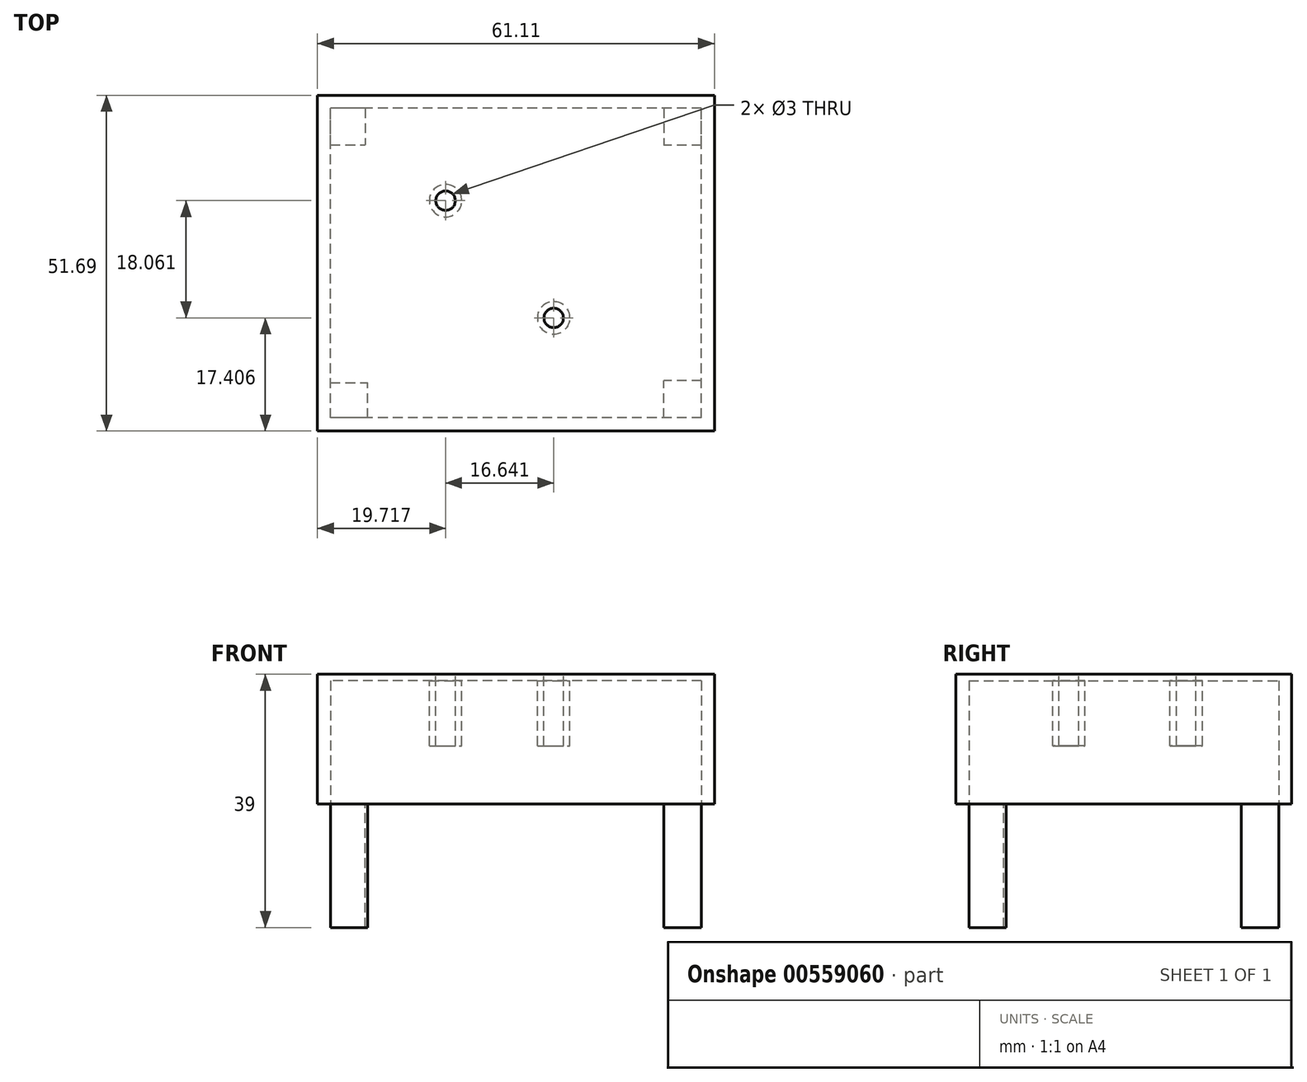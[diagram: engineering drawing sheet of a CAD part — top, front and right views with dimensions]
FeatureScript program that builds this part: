
annotation { "Feature Type Name" : "Feature", "Feature Type Description" : "" }
export const myFeature = defineFeature(function(context is Context, id is Id, definition is map)
    precondition{}
    {
        {
            var Q0;
            Q0=qCreatedBy(makeId("Top.planeOp"),FACE);
            var sketch = newSketch(context, id + "F0", { "sketchPlane" : qUnion([Q0])});
            skLineSegment(sketch, "E0.bottom", {"start": v(-30.7, 24.9) * mm, "end": v(30.42, 24.9) * mm});
            skLineSegment(sketch, "E0.top", {"start": v(-30.7, -26.79) * mm, "end": v(30.42, -26.79) * mm});
            skLineSegment(sketch, "E0.left", {"start": v(-30.7, 24.9) * mm, "end": v(-30.7, -26.79) * mm});
            skLineSegment(sketch, "E0.right", {"start": v(30.42, 24.9) * mm, "end": v(30.42, -26.79) * mm});
            skSolve(sketch);
        }
        {
            var Q0;
            Q0=makeQuery(id+"F0.imprint","IMPRINT",FACE,{"disambiguationData":[TD([[makeQuery(id+"F0.imprint","IMPRINT",EDGE,{"derivedFrom":sQuery(id+"F0.wireOp",EDGE,"E0.bottom")}),-1.0]])]});
            extrude(context, id + "F1", {"entities" : qUnion([Q0]), "depth" : 20 * mm, "offsetDistance" : 25 * mm});
        }
        {
            var Q0;
            Q0=makeQuery(id+"F1.opExtrude","CAP_FACE",FACE,{"disambiguationData":[OSD([sQuery(id+"F0.wireOp",EDGE,"E0.bottom"),sQuery(id+"F0.wireOp",EDGE,"E0.top"),sQuery(id+"F0.wireOp",EDGE,"E0.left"),sQuery(id+"F0.wireOp",EDGE,"E0.right")])],"isStart":true});
            var sketch = newSketch(context, id + "F2", { "sketchPlane" : qUnion([Q0])});
            skLineSegment(sketch, "E1.bottom", {"start": v(28.42, 24.79) * mm, "end": v(-28.7, 24.79) * mm});
            skLineSegment(sketch, "E1.top", {"start": v(28.42, -22.9) * mm, "end": v(-28.7, -22.9) * mm});
            skLineSegment(sketch, "E1.left", {"start": v(28.42, 24.79) * mm, "end": v(28.42, -22.9) * mm});
            skLineSegment(sketch, "E1.right", {"start": v(-28.7, 24.79) * mm, "end": v(-28.7, -22.9) * mm});
            skSolve(sketch);
        }
        {
            var Q0;
            Q0=makeQuery(id+"F2.imprint","IMPRINT",FACE,{"disambiguationData":[TD([[makeQuery(id+"F2.imprint","IMPRINT",EDGE,{"derivedFrom":sQuery(id+"F2.wireOp",EDGE,"E1.bottom")}),1.0]])]});
            extrude(context, id + "F3", {"entities" : qUnion([Q0]), "operationType" : NewBodyOperationType.REMOVE, "oppositeDirection" : true, "depth" : 19 * mm, "offsetDistance" : 25 * mm});
        }
        {
            var Q0;
            Q0=makeQuery(id+"F3.boolean.opBoolean","COPY",FACE,{"derivedFrom":makeQuery(id+"F3.opExtrude","CAP_FACE",FACE,{"disambiguationData":[OSD([sQuery(id+"F2.wireOp",EDGE,"E1.bottom"),sQuery(id+"F2.wireOp",EDGE,"E1.top"),sQuery(id+"F2.wireOp",EDGE,"E1.left"),sQuery(id+"F2.wireOp",EDGE,"E1.right")])],"isStart":false})});
            var sketch = newSketch(context, id + "F4", { "sketchPlane" : qUnion([Q0])});
            skCircle(sketch, "E2", {"center": v(5.67, 9.38) * mm, "radius": 1.5 * mm});
            skCircle(sketch, "E3", {"center": v(-10.97, -8.68) * mm, "radius": 1.5 * mm});
            skCircle(sketch, "E4", {"center": v(-10.97, -8.68) * mm, "radius": 2.5 * mm});
            skCircle(sketch, "E5", {"center": v(5.67, 9.38) * mm, "radius": 2.5 * mm});
            skSolve(sketch);
        }
        {
            var Q0;
            Q0 = qSketchRegion(id + "F4", true);
            extrude(context, id + "F5", {"entities" : qUnion([Q0]), "operationType" : NewBodyOperationType.ADD, "depth" : 10 * mm, "offsetDistance" : 25 * mm});
        }
        {
            var Q0;
            Q0=makeQuery(id+"F5.boolean.opBoolean","SPLIT",FACE,{"disambiguationData":[TD([makeQuery(id+"F5.opExtrude","SWEPT_FACE",FACE,{"disambiguationData":[OSD([sQuery(id+"F4.wireOp",EDGE,"E3")])]})])],"derivedFrom":makeQuery(id+"F3.boolean.opBoolean","COPY",FACE,{"derivedFrom":makeQuery(id+"F3.opExtrude","CAP_FACE",FACE,{"disambiguationData":[OSD([sQuery(id+"F2.wireOp",EDGE,"E1.bottom"),sQuery(id+"F2.wireOp",EDGE,"E1.top"),sQuery(id+"F2.wireOp",EDGE,"E1.left"),sQuery(id+"F2.wireOp",EDGE,"E1.right")])],"isStart":false})})});
            var Q1;
            Q1=makeQuery(id+"F5.boolean.opBoolean","SPLIT",FACE,{"disambiguationData":[TD([makeQuery(id+"F5.opExtrude","SWEPT_FACE",FACE,{"disambiguationData":[OSD([sQuery(id+"F4.wireOp",EDGE,"E2")])]})])],"derivedFrom":makeQuery(id+"F3.boolean.opBoolean","COPY",FACE,{"derivedFrom":makeQuery(id+"F3.opExtrude","CAP_FACE",FACE,{"disambiguationData":[OSD([sQuery(id+"F2.wireOp",EDGE,"E1.bottom"),sQuery(id+"F2.wireOp",EDGE,"E1.top"),sQuery(id+"F2.wireOp",EDGE,"E1.left"),sQuery(id+"F2.wireOp",EDGE,"E1.right")])],"isStart":false})})});
            extrude(context, id + "F6", {"entities" : qUnion([Q0, Q1]), "operationType" : NewBodyOperationType.REMOVE, "oppositeDirection" : true, "depth" : 1 * mm, "offsetDistance" : 25 * mm});
        }
        {
            var Q0;
            Q0=makeQuery(id+"F1.opExtrude","CAP_FACE",FACE,{"disambiguationData":[OSD([sQuery(id+"F0.wireOp",EDGE,"E0.bottom"),sQuery(id+"F0.wireOp",EDGE,"E0.top"),sQuery(id+"F0.wireOp",EDGE,"E0.left"),sQuery(id+"F0.wireOp",EDGE,"E0.right")])],"isStart":true});
            var sketch = newSketch(context, id + "F7", { "sketchPlane" : qUnion([Q0])});
            skLineSegment(sketch, "E6.bottom", {"start": v(-28.7, 24.79) * mm, "end": v(-22.98, 24.79) * mm});
            skLineSegment(sketch, "E6.top", {"start": v(-28.7, 19.4) * mm, "end": v(-22.98, 19.4) * mm});
            skLineSegment(sketch, "E6.left", {"start": v(-28.7, 24.79) * mm, "end": v(-28.7, 19.4) * mm});
            skLineSegment(sketch, "E6.right", {"start": v(-22.98, 24.79) * mm, "end": v(-22.98, 19.4) * mm});
            skLineSegment(sketch, "E7.bottom", {"start": v(-28.7, -22.9) * mm, "end": v(-23.34, -22.9) * mm});
            skLineSegment(sketch, "E7.top", {"start": v(-28.7, -17.3) * mm, "end": v(-23.34, -17.3) * mm});
            skLineSegment(sketch, "E7.left", {"start": v(-28.7, -22.9) * mm, "end": v(-28.7, -17.3) * mm});
            skLineSegment(sketch, "E7.right", {"start": v(-23.34, -22.9) * mm, "end": v(-23.34, -17.3) * mm});
            skLineSegment(sketch, "E8.bottom", {"start": v(28.42, -22.9) * mm, "end": v(22.6, -22.9) * mm});
            skLineSegment(sketch, "E8.top", {"start": v(28.42, -17.18) * mm, "end": v(22.6, -17.18) * mm});
            skLineSegment(sketch, "E8.left", {"start": v(28.42, -22.9) * mm, "end": v(28.42, -17.18) * mm});
            skLineSegment(sketch, "E8.right", {"start": v(22.6, -22.9) * mm, "end": v(22.6, -17.18) * mm});
            skLineSegment(sketch, "E9.bottom", {"start": v(28.42, 24.79) * mm, "end": v(22.6, 24.79) * mm});
            skLineSegment(sketch, "E9.top", {"start": v(28.42, 19.04) * mm, "end": v(22.6, 19.04) * mm});
            skLineSegment(sketch, "E9.left", {"start": v(28.42, 24.79) * mm, "end": v(28.42, 19.04) * mm});
            skLineSegment(sketch, "E9.right", {"start": v(22.6, 24.79) * mm, "end": v(22.6, 19.04) * mm});
            skSolve(sketch);
        }
        {
            var Q0;
            Q0 = qSketchRegion(id + "F7", true);
            extrude(context, id + "F8", {"entities" : qUnion([Q0]), "operationType" : NewBodyOperationType.ADD, "depth" : 19 * mm, "offsetDistance" : 25 * mm});
        }
    });
